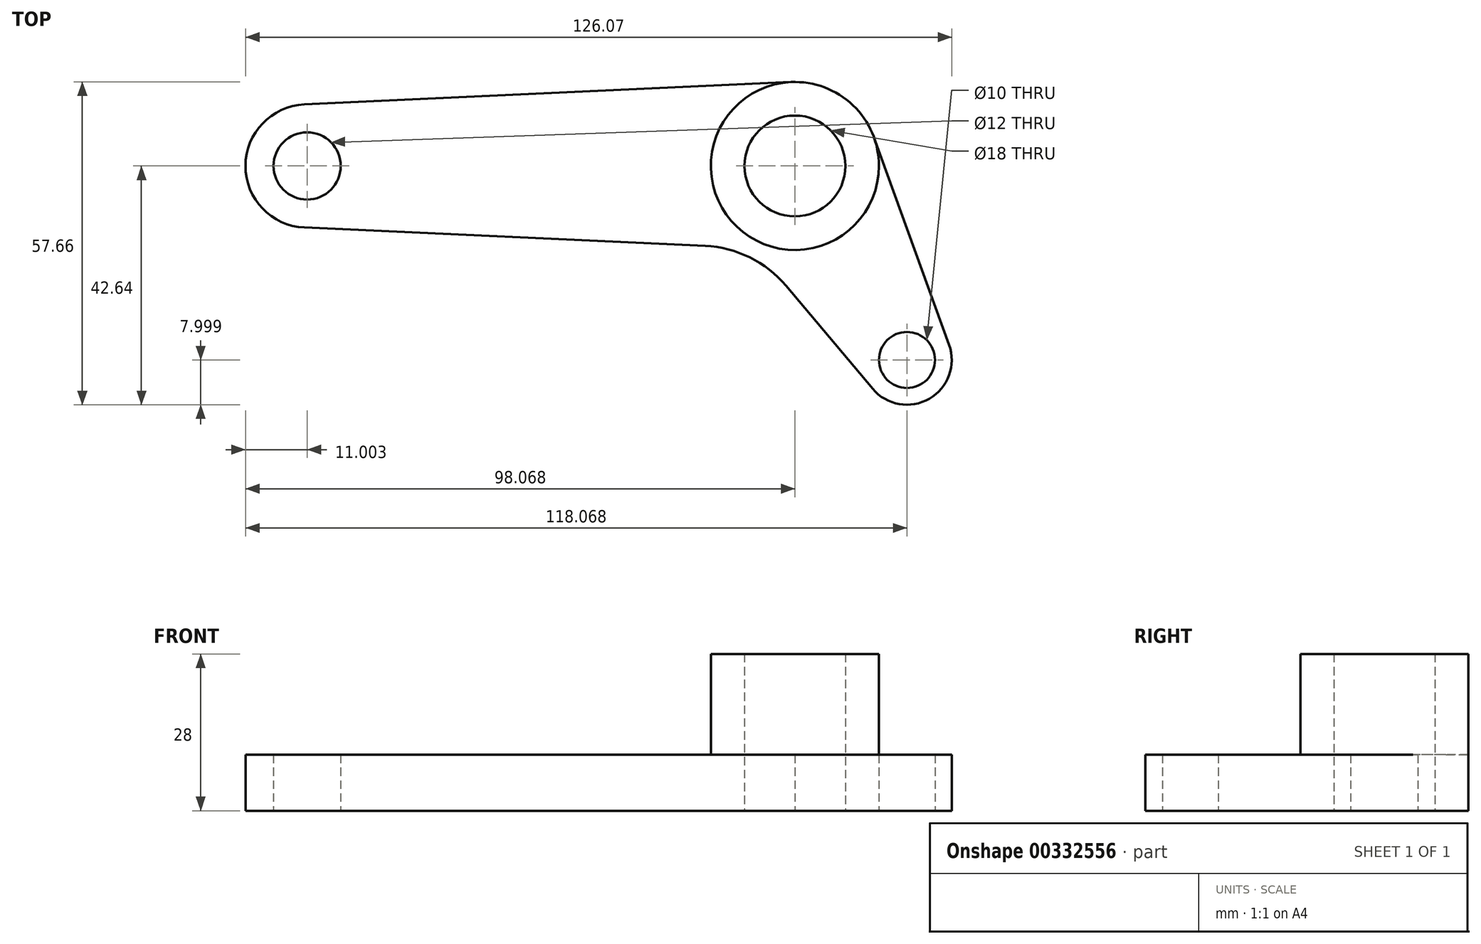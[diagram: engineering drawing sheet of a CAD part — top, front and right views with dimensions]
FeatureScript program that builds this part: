
annotation { "Feature Type Name" : "Feature", "Feature Type Description" : "" }
export const myFeature = defineFeature(function(context is Context, id is Id, definition is map)
    precondition{}
    {
        {
            var Q0;
            Q0=qCreatedBy(makeId("Top.planeOp"),FACE);
            var sketch = newSketch(context, id + "F0", { "sketchPlane" : qUnion([Q0])});
            skCircle(sketch, "E0", {"center": v(-41.09, 0) * mm, "radius": 6 * mm});
            skCircle(sketch, "E1", {"center": v(-41.09, 0) * mm, "radius": 11 * mm});
            skCircle(sketch, "E2", {"center": v(45.98, 0) * mm, "radius": 9 * mm});
            skCircle(sketch, "E3", {"center": v(45.98, 0) * mm, "radius": 15 * mm});
            skLineSegment(sketch, "E4", {"start": v(45.98, 15.02) * mm, "end": v(45.98, 15) * mm});
            skPoint(sketch, "E5", {"position": v(65.98, -34.64) * mm});
            skPoint(sketch, "E6", {"position": v(81.74, 35.75) * mm});
            skPoint(sketch, "E7", {"position": v(-11.53, -91.2) * mm});
            skPoint(sketch, "E8", {"position": v(88.16, -67.64) * mm});
            skPoint(sketch, "E9", {"position": v(65.98, 57.1) * mm});
            skPoint(sketch, "E10", {"position": v(64.38, 63.54) * mm});
            skCircle(sketch, "E11", {"center": v(65.98, -34.64) * mm, "radius": 5 * mm});
            skCircle(sketch, "E12", {"center": v(65.98, -34.64) * mm, "radius": 8 * mm});
            skLineSegment(sketch, "E13", {"start": v(-44.7, 10.85) * mm, "end": v(45.98, 15.02) * mm});
            skLineSegment(sketch, "E14", {"start": v(-41.6, -10.99) * mm, "end": v(29.98, -14.28) * mm});
            skLineSegment(sketch, "E15", {"start": v(44.37, -21.38) * mm, "end": v(59.86, -39.8) * mm});
            skLineSegment(sketch, "E16", {"start": v(60.08, 5.11) * mm, "end": v(73.5, -31.92) * mm});
            skArc(sketch, "E17.filletArc", {"start": v(44.37, -21.38) * mm, "mid": v(37.92, -16.33) * mm, "end": v(29.98, -14.28) * mm});
            skPoint(sketch, "E18.orphan", {"position": v(45.98, 43.45) * mm});
            skLineSegment(sketch, "E19.trimOffspring", {"start": v(45.98, -9) * mm, "end": v(45.98, -40.94) * mm});
            skPoint(sketch, "E20.trimOffspring.end.orphan", {"position": v(69.61, -40.94) * mm});
            skSolve(sketch);
        }
        {
            var Q0;
            {var subQ0=sQuery(id+"F0.wireOp",EDGE,"E4");Q0=makeQuery(id+"F0.imprint","IMPRINT",FACE,{"disambiguationData":[TD([[makeQuery(id+"F0.imprint","IMPRINT",EDGE,{"derivedFrom":subQ0}),-1.0]])]});}
            var Q1;
            Q1=makeQuery(id+"F0.imprint","IMPRINT",FACE,{"disambiguationData":[TD([[makeQuery(id+"F0.imprint","IMPRINT",EDGE,{"derivedFrom":sQuery(id+"F0.wireOp",EDGE,"E0")}),-1.0]])]});
            var Q2;
            Q2=makeQuery(id+"F0.imprint","IMPRINT",FACE,{"disambiguationData":[TD([[makeQuery(id+"F0.imprint","IMPRINT",EDGE,{"derivedFrom":sQuery(id+"F0.wireOp",EDGE,"E11")}),-1.0]])]});
            var Q3;
            {var subQ0=sQuery(id+"F0.wireOp",EDGE,"E14");Q3=makeQuery(id+"F0.imprint","IMPRINT",FACE,{"disambiguationData":[TD([[makeQuery(id+"F0.imprint","IMPRINT",EDGE,{"derivedFrom":subQ0}),1.0]])]});}
            var Q4;
            {var subQ5=sQuery(id+"F0.wireOp",EDGE,"E16");Q4=makeQuery(id+"F0.imprint","IMPRINT",FACE,{"disambiguationData":[TD([[makeQuery(id+"F0.imprint","IMPRINT",EDGE,{"derivedFrom":subQ5}),-1.0]])]});}
            var Q5;
            Q5=makeQuery(id+"F0.imprint","IMPRINT",FACE,{"disambiguationData":[TD([[makeQuery(id+"F0.imprint","IMPRINT",EDGE,{"derivedFrom":sQuery(id+"F0.wireOp",EDGE,"E2")}),-1.0]])]});
            extrude(context, id + "F1", {"entities" : qUnion([Q0, Q1, Q2, Q3, Q4, Q5]), "depth" : 10 * mm});
        }
        {
            var Q0;
            Q0=makeQuery(id+"F0.imprint","IMPRINT",FACE,{"disambiguationData":[TD([[makeQuery(id+"F0.imprint","IMPRINT",EDGE,{"derivedFrom":sQuery(id+"F0.wireOp",EDGE,"E2")}),-1.0]])]});
            extrude(context, id + "F2", {"entities" : qUnion([Q0]), "operationType" : NewBodyOperationType.ADD, "depth" : 28 * mm});
        }
    });
